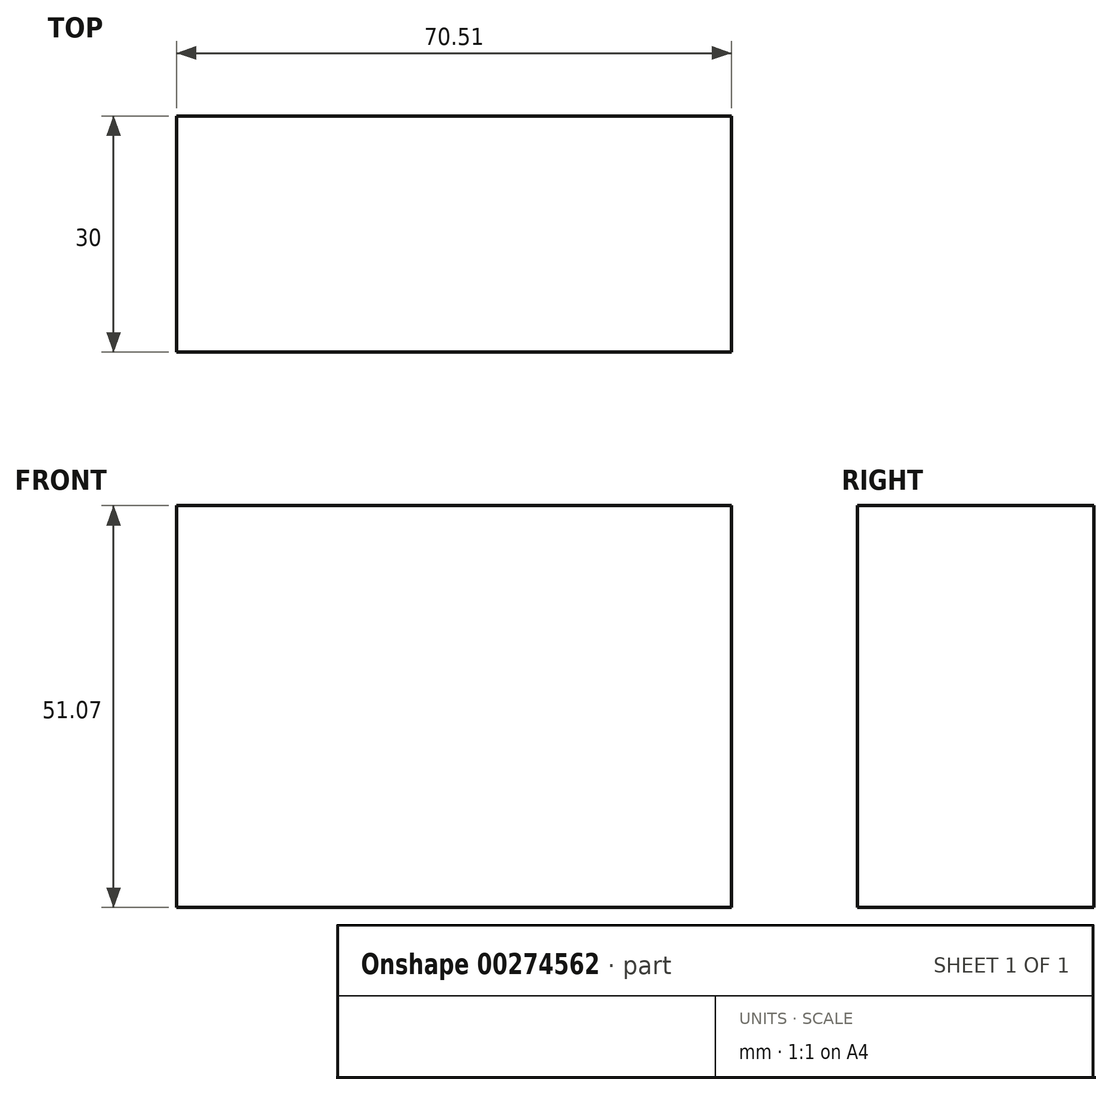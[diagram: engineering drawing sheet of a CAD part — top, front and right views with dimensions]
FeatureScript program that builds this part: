
annotation { "Feature Type Name" : "Feature", "Feature Type Description" : "" }
export const myFeature = defineFeature(function(context is Context, id is Id, definition is map)
    precondition{}
    {
        {
            var Q0;
            Q0=qCreatedBy(makeId("Front.planeOp"),FACE);
            var sketch = newSketch(context, id + "F0", { "sketchPlane" : qUnion([Q0])});
            skLineSegment(sketch, "E0.bottom", {"start": v(0, 0) * mm, "end": v(70.51, 0) * mm});
            skLineSegment(sketch, "E0.top", {"start": v(0, -51.07) * mm, "end": v(70.51, -51.07) * mm});
            skLineSegment(sketch, "E0.left", {"start": v(0, 0) * mm, "end": v(0, -51.07) * mm});
            skLineSegment(sketch, "E0.right", {"start": v(70.51, 0) * mm, "end": v(70.51, -51.07) * mm});
            skSolve(sketch);
        }
        {
            var Q0;
            Q0=qSketchRegion(id+"F0",true);
            extrude(context, id + "F1", {"entities" : qUnion([Q0]), "depth" : 30 * mm});
        }
    });
